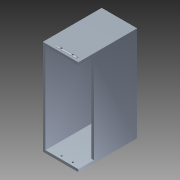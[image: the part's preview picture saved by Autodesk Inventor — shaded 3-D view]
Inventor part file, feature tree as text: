
AUTODESK INVENTOR PART (.ipt)
format: ipt  version: 2015 (Build 190159000, 159)  size: 220,672 bytes
history: native  units: in
note: dims shown in document units (in); Inventor stores cm internally (conversion verified against a paired STEP export)
features: sketch x3, extrude x2, direct_edit x2, projected_geometry x2, move_body x2, imported_body x1
ambient origin geometry x8: Origin, YZ Plane, XZ Plane, XY Plane, X Axis, Y Axis, Z Axis, Center Point
bodies: Solid1 (feature_tree)
feature tree (12):
  imported_body  "Base1"
  sketch  "Sketch2"  dims[d0=30.0in d1=0.0in d2=30.0in d3=0.0in]
  extrude  "Extrusion1"  Depth=30.0in TaperAngle=0.0deg
  extrude  "Extrusion2"  Depth=30.0in TaperAngle=0.0deg
  direct_edit  "Direct Edit3"
  direct_edit  "Direct Edit4"
  sketch  "Sketch3"  dims[d10=0.0in d11=30.0in d12=0.0in d13=0.0in d14=30.0in d15=0.0in]
  projected_geometry  "Projected Loop1"
  sketch  "Sketch4"
  projected_geometry  "Projected Loop2"
  move_body  "Move3"
  move_body  "Move4"
